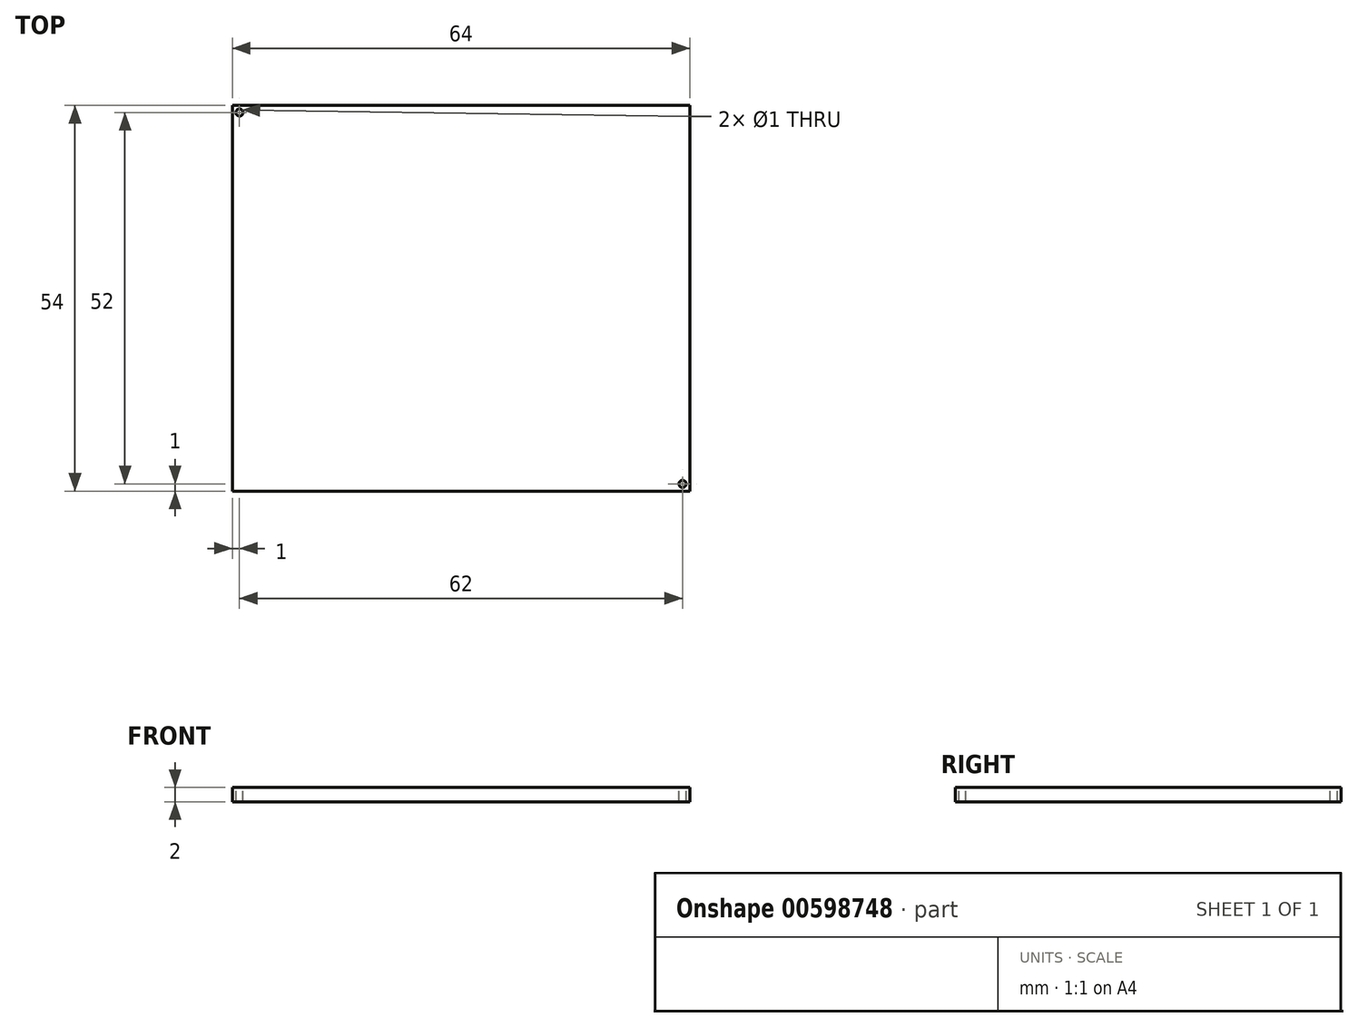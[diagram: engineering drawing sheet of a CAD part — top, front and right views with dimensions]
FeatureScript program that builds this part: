
annotation { "Feature Type Name" : "Feature", "Feature Type Description" : "" }
export const myFeature = defineFeature(function(context is Context, id is Id, definition is map)
    precondition{}
    {
        {
            var Q0;
            Q0=qCreatedBy(makeId("Top.planeOp"),FACE);
            var sketch = newSketch(context, id + "F0", { "sketchPlane" : qUnion([Q0])});
            skLineSegment(sketch, "E0.bottom", {"start": v(-32, 27) * mm, "end": v(32, 27) * mm});
            skLineSegment(sketch, "E0.top", {"start": v(-32, -27) * mm, "end": v(32, -27) * mm});
            skLineSegment(sketch, "E0.left", {"start": v(-32, 27) * mm, "end": v(-32, -27) * mm});
            skLineSegment(sketch, "E0.right", {"start": v(32, 27) * mm, "end": v(32, -27) * mm});
            skPoint(sketch, "E0.middle", {"position": v(0, 0) * mm});
            skSolve(sketch);
        }
        {
            var Q0;
            Q0=makeQuery(id+"F0.imprint","IMPRINT",FACE,{"disambiguationData":[TD([[makeQuery(id+"F0.imprint","IMPRINT",EDGE,{"derivedFrom":sQuery(id+"F0.wireOp",EDGE,"E0.bottom")}),-1.0]])]});
            extrude(context, id + "F1", {"entities" : qUnion([Q0]), "depth" : 2 * mm, "offsetDistance" : 25.4 * mm});
        }
        {
            var Q0;
            Q0=makeQuery(id+"F1.opExtrude","CAP_FACE",FACE,{"disambiguationData":[OSD([sQuery(id+"F0.wireOp",EDGE,"E0.bottom"),sQuery(id+"F0.wireOp",EDGE,"E0.top"),sQuery(id+"F0.wireOp",EDGE,"E0.left"),sQuery(id+"F0.wireOp",EDGE,"E0.right")])],"isStart":false});
            var sketch = newSketch(context, id + "F2", { "sketchPlane" : qUnion([Q0])});
            skLineSegment(sketch, "E1", {"start": v(-32, 27) * mm, "end": v(-30, 27) * mm});
            skLineSegment(sketch, "E2", {"start": v(-32, 27) * mm, "end": v(-32, 25) * mm});
            skLineSegment(sketch, "E3", {"start": v(-32, 25) * mm, "end": v(-30, 27) * mm});
            skLineSegment(sketch, "E4", {"start": v(-32, 27) * mm, "end": v(-31, 26) * mm});
            skPoint(sketch, "E5", {"position": v(-31, 26) * mm});
            skCircle(sketch, "E6", {"center": v(-31, 26) * mm, "radius": 0.5 * mm});
            skSolve(sketch);
        }
        {
            var Q0;
            Q0=makeQuery(id+"F1.opExtrude","CAP_FACE",FACE,{"disambiguationData":[OSD([sQuery(id+"F0.wireOp",EDGE,"E0.bottom"),sQuery(id+"F0.wireOp",EDGE,"E0.top"),sQuery(id+"F0.wireOp",EDGE,"E0.left"),sQuery(id+"F0.wireOp",EDGE,"E0.right")])],"isStart":false});
            var sketch = newSketch(context, id + "F3", { "sketchPlane" : qUnion([Q0])});
            skLineSegment(sketch, "E7", {"start": v(32, -27) * mm, "end": v(32, -25) * mm});
            skLineSegment(sketch, "E8", {"start": v(32, -27) * mm, "end": v(30, -27) * mm});
            skLineSegment(sketch, "E9", {"start": v(30, -27) * mm, "end": v(32, -25) * mm});
            skLineSegment(sketch, "E10", {"start": v(32, -27) * mm, "end": v(31, -26) * mm});
            skPoint(sketch, "E11", {"position": v(31, -26) * mm});
            skSolve(sketch);
        }
        {
            var Q0;
            Q0=sQuery(id+"F3.wireOp",VERTEX,"E11");
            var Q1;
            Q1=makeQuery(id+"F1.opExtrude","SWEPT_BODY",BODY,{"disambiguationData":[OSD([sQuery(id+"F0.wireOp",EDGE,"E0.bottom"),sQuery(id+"F0.wireOp",EDGE,"E0.top"),sQuery(id+"F0.wireOp",EDGE,"E0.left"),sQuery(id+"F0.wireOp",EDGE,"E0.right")])]});
            hole(context, id + "F4", {"style" : HoleStyle.SIMPLE, "endStyle" : HoleEndStyle.THROUGH, "holeDiameter" : 1 * mm, "majorDiameter" : 6.35 * mm, "isTappedThrough" : true, "tappedDepth" : 12.7 * mm, "tapClearance" : 3, "locations" : qUnion([Q0]), "scope" : qUnion([Q1])});
        }
        {
            var Q0;
            Q0=sQuery(id+"F2.wireOp",VERTEX,"E5");
            var Q1;
            Q1=makeQuery(id+"F1.opExtrude","SWEPT_BODY",BODY,{"disambiguationData":[OSD([sQuery(id+"F0.wireOp",EDGE,"E0.bottom"),sQuery(id+"F0.wireOp",EDGE,"E0.top"),sQuery(id+"F0.wireOp",EDGE,"E0.left"),sQuery(id+"F0.wireOp",EDGE,"E0.right")])]});
            hole(context, id + "F5", {"style" : HoleStyle.SIMPLE, "endStyle" : HoleEndStyle.THROUGH, "holeDiameter" : 1 * mm, "majorDiameter" : 6.35 * mm, "isTappedThrough" : true, "tappedDepth" : 12.7 * mm, "tapClearance" : 3, "locations" : qUnion([Q0]), "scope" : qUnion([Q1])});
        }
    });
